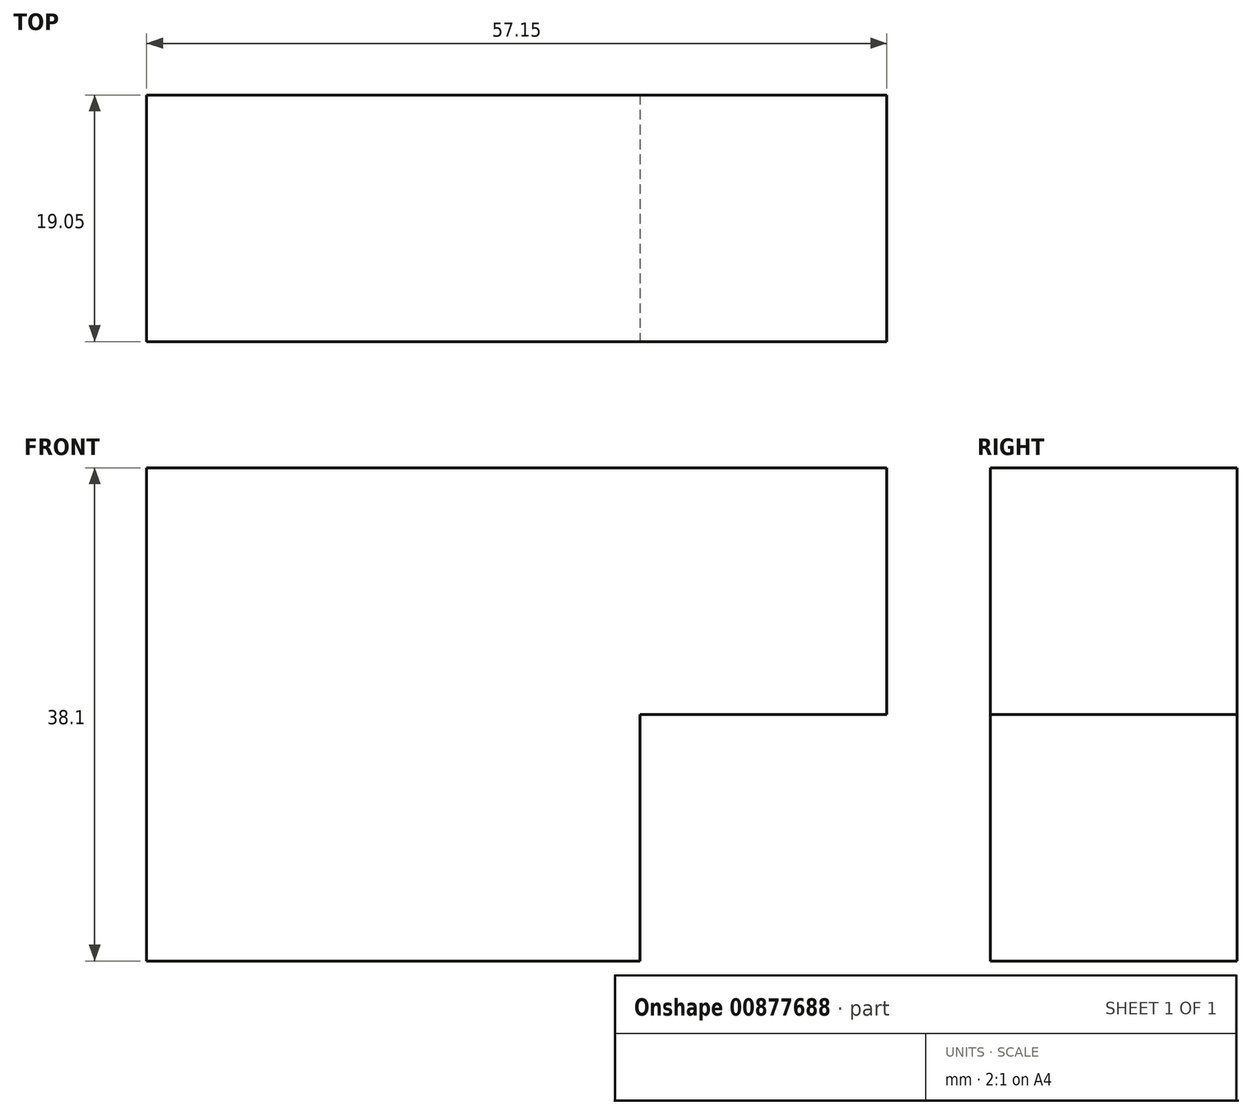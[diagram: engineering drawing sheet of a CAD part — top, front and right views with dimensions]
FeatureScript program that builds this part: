
annotation { "Feature Type Name" : "Feature", "Feature Type Description" : "" }
export const myFeature = defineFeature(function(context is Context, id is Id, definition is map)
    precondition{}
    {
        {
            var Q0;
            Q0=qCreatedBy(makeId("Top.planeOp"),FACE);
            cPlane(context, id + "F0", {"entities" : qUnion([Q0]), "cplaneType" : CPlaneType.OFFSET, "offset" : 25.4 * mm, "width" : 152.4 * mm, "height" : 152.4 * mm});
        }
        {
            var Q0;
            Q0=qCreatedBy(id+"F0.planeOp",FACE);
            var sketch = newSketch(context, id + "F1", { "sketchPlane" : qUnion([Q0])});
            skLineSegment(sketch, "E0.bottom", {"start": v(0, -38.1) * mm, "end": v(38.1, -38.1) * mm});
            skLineSegment(sketch, "E0.top", {"start": v(0, -57.15) * mm, "end": v(38.1, -57.15) * mm});
            skLineSegment(sketch, "E0.left", {"start": v(0, -38.1) * mm, "end": v(0, -57.15) * mm});
            skLineSegment(sketch, "E0.right", {"start": v(38.1, -38.1) * mm, "end": v(38.1, -57.15) * mm});
            skSolve(sketch);
        }
        {
            var Q0;
            Q0=qSketchRegion(id+"F1",true);
            extrude(context, id + "F2", {"entities" : qUnion([Q0]), "depth" : 19.05 * mm});
        }
        {
            var Q0;
            Q0=makeQuery(id+"F2.opExtrude","CAP_FACE",FACE,{"disambiguationData":[OSD([sQuery(id+"F1.wireOp",EDGE,"E0.bottom"),sQuery(id+"F1.wireOp",EDGE,"E0.top"),sQuery(id+"F1.wireOp",EDGE,"E0.left"),sQuery(id+"F1.wireOp",EDGE,"E0.right")])],"isStart":false});
            var sketch = newSketch(context, id + "F3", { "sketchPlane" : qUnion([Q0])});
            skLineSegment(sketch, "E1.bottom", {"start": v(0, -57.15) * mm, "end": v(57.15, -57.15) * mm});
            skLineSegment(sketch, "E1.top", {"start": v(0, -38.1) * mm, "end": v(57.15, -38.1) * mm});
            skLineSegment(sketch, "E1.left", {"start": v(0, -57.15) * mm, "end": v(0, -38.1) * mm});
            skLineSegment(sketch, "E1.right", {"start": v(57.15, -57.15) * mm, "end": v(57.15, -38.1) * mm});
            skSolve(sketch);
        }
        {
            var Q0;
            Q0=qSketchRegion(id+"F3",true);
            extrude(context, id + "F4", {"entities" : qUnion([Q0]), "operationType" : NewBodyOperationType.ADD, "depth" : 19.05 * mm});
        }
    });
